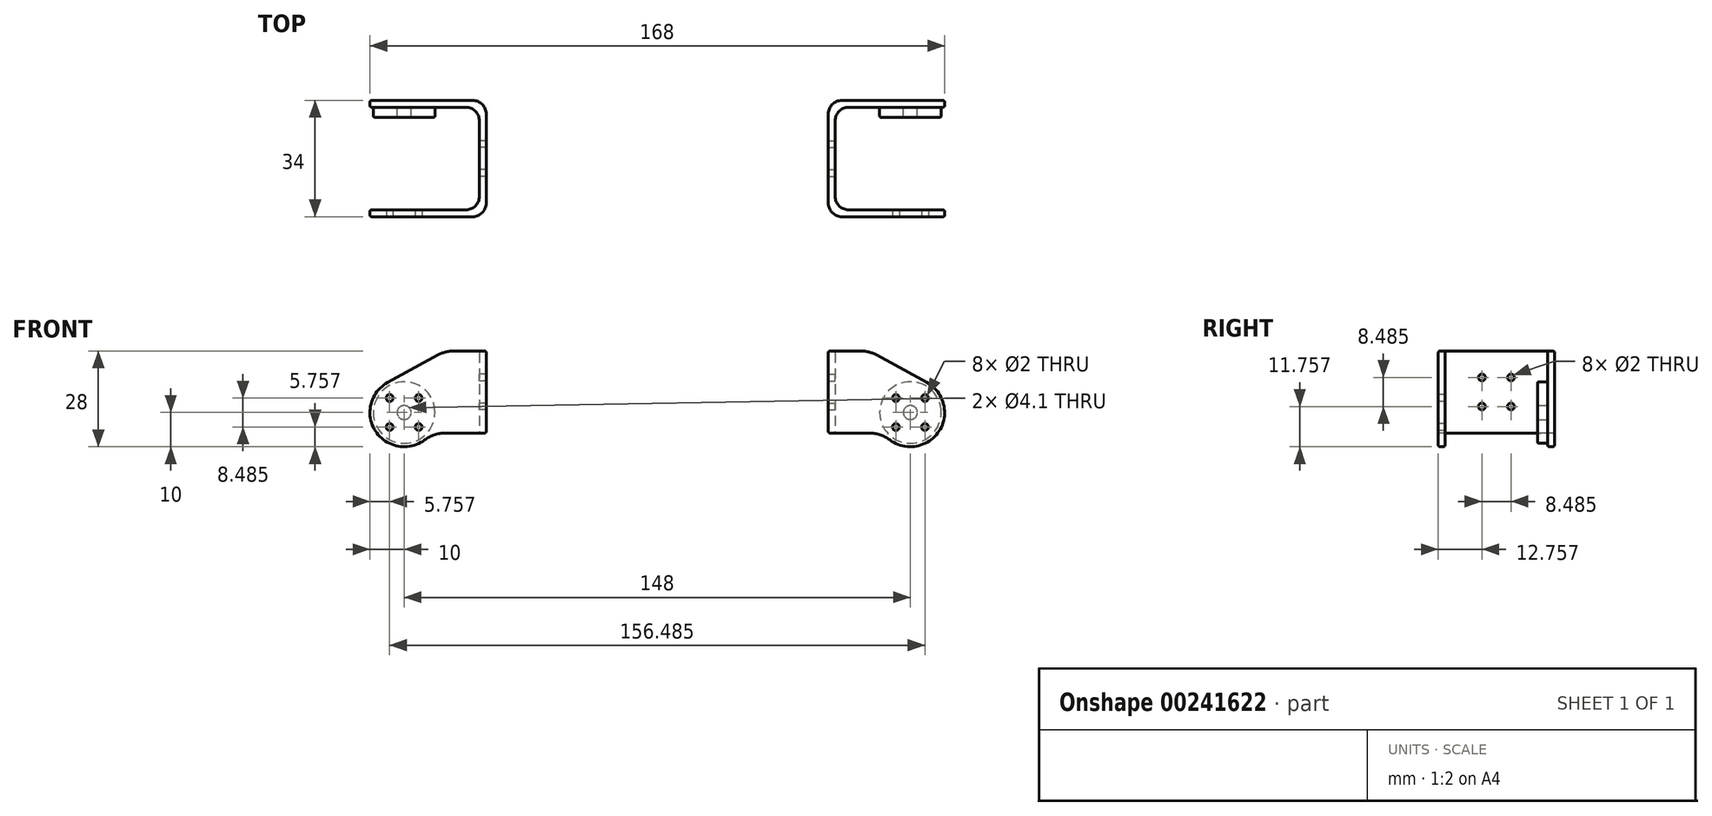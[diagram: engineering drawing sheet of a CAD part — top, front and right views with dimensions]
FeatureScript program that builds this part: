
annotation { "Feature Type Name" : "Feature", "Feature Type Description" : "" }
export const myFeature = defineFeature(function(context is Context, id is Id, definition is map)
    precondition{}
    {
        {
            var Q0;
            Q0=qCreatedBy(makeId("Front.planeOp"),FACE);
            var sketch = newSketch(context, id + "F0", { "sketchPlane" : qUnion([Q0])});
            skCircle(sketch, "E0", {"center": v(24, -6) * mm, "radius": 10 * mm});
            skLineSegment(sketch, "E1.bottom", {"start": v(0, 12) * mm, "end": v(24, 12) * mm});
            skLineSegment(sketch, "E1.top", {"start": v(0, -12) * mm, "end": v(24, -12) * mm});
            skLineSegment(sketch, "E1.left", {"start": v(0, 12) * mm, "end": v(0, -12) * mm});
            skLineSegment(sketch, "E1.right", {"start": v(24, 12) * mm, "end": v(24, -12) * mm});
            skLineSegment(sketch, "E2", {"start": v(12, 12) * mm, "end": v(30.55, 1.81) * mm});
            skSolve(sketch);
        }
        {
            var Q0;
            {var subQ0=sQuery(id+"F0.wireOp",EDGE,"E0");var subQ1=makeQuery(id+"F0.imprint","INTERSECT",VERTEX,{"derivedFrom":[subQ0,sQuery(id+"F0.wireOp",EDGE,"E2")]});Q0=makeQuery(id+"F0.imprint","IMPRINT",FACE,{"disambiguationData":[TD([[makeQuery(id+"F0.imprint","IMPRINT",EDGE,{"disambiguationData":[TD([[subQ1,-1.0]])],"derivedFrom":subQ0}),1.0]])]});}
            var Q1;
            {var subQ0=sQuery(id+"F0.wireOp",EDGE,"E2");var subQ1=sQuery(id+"F0.wireOp",EDGE,"E0");var subQ2=makeQuery(id+"F0.imprint","INTERSECT",VERTEX,{"derivedFrom":[subQ1,subQ0]});Q1=makeQuery(id+"F0.imprint","IMPRINT",FACE,{"disambiguationData":[TD([[makeQuery(id+"F0.imprint","IMPRINT",EDGE,{"disambiguationData":[TD([[subQ2,-1.0]])],"derivedFrom":subQ1}),-1.0]])]});}
            var Q2;
            {var subQ0=sQuery(id+"F0.wireOp",EDGE,"E1.top");var subQ1=sQuery(id+"F0.wireOp",EDGE,"E0");var subQ2=makeQuery(id+"F0.imprint","INTERSECT",VERTEX,{"derivedFrom":[subQ1,subQ0]});Q2=makeQuery(id+"F0.imprint","IMPRINT",FACE,{"disambiguationData":[TD([[makeQuery(id+"F0.imprint","IMPRINT",EDGE,{"disambiguationData":[TD([[subQ2,1.0]])],"derivedFrom":subQ1}),1.0]])]});}
            var Q3;
            {var subQ0=sQuery(id+"F0.wireOp",EDGE,"E1.left");Q3=makeQuery(id+"F0.imprint","IMPRINT",FACE,{"disambiguationData":[TD([[makeQuery(id+"F0.imprint","IMPRINT",EDGE,{"derivedFrom":subQ0}),1.0]])]});}
            extrude(context, id + "F1", {"entities" : qUnion([Q0, Q1, Q2, Q3]), "depth" : 17 * mm, "hasSecondDirection" : true, "secondDirectionOppositeDirection" : true, "secondDirectionDepth" : 17 * mm});
        }
        {
            var Q0;
            Q0=makeQuery(id+"F1.opExtrude","SWEPT_EDGE",EDGE,{"disambiguationData":[OSD([sQuery(id+"F0.wireOp",EDGE,"E1.bottom"),sQuery(id+"F0.wireOp",EDGE,"E2")])]});
            var Q1;
            Q1=makeQuery(id+"F1.opExtrude","SWEPT_EDGE",EDGE,{"disambiguationData":[OSD([sQuery(id+"F0.wireOp",EDGE,"E0"),sQuery(id+"F0.wireOp",EDGE,"E1.top")])]});
            fillet(context, id + "F2", {"entities" : qUnion([Q0, Q1]), "radius" : 10 * mm, "tangentPropagation" : true, "allowEdgeOverflow" : false});
        }
        {
            var Q0;
            Q0=makeQuery(id+"F1.opExtrude","SWEPT_FACE",FACE,{"disambiguationData":[OSD([sQuery(id+"F0.wireOp",EDGE,"q71L5gfp-R8vq-MGxF-tGWS-dWD6cUmfp0Zf")])]});
            var Q1;
            Q1=makeQuery(id+"F2.opFillet","BLEND_FACE",FACE,{"disambiguationData":[OSD([sQuery(id+"F0.wireOp",EDGE,"E1.bottom"),sQuery(id+"F0.wireOp",EDGE,"E1.right"),sQuery(id+"F0.wireOp",EDGE,"q71L5gfp-R8vq-MGxF-tGWS-dWD6cUmfp0Zf")])]});
            var Q2;
            Q2=makeQuery(id+"F1.opExtrude","SWEPT_FACE",FACE,{"disambiguationData":[OSD([sQuery(id+"F0.wireOp",EDGE,"E1.bottom")])]});
            var Q3;
            Q3=makeQuery(id+"F1.opExtrude","SWEPT_FACE",FACE,{"disambiguationData":[OSD([sQuery(id+"F0.wireOp",EDGE,"E0")])]});
            var Q4;
            Q4=makeQuery(id+"F2.opFillet","BLEND_FACE",FACE,{"disambiguationData":[OSD([sQuery(id+"F0.wireOp",EDGE,"E0"),sQuery(id+"F0.wireOp",EDGE,"E1.top")])]});
            var Q5;
            Q5=makeQuery(id+"F1.opExtrude","SWEPT_FACE",FACE,{"disambiguationData":[OSD([sQuery(id+"F0.wireOp",EDGE,"E1.top")])]});
            var Q6;
            Q6=makeQuery(id+"F1.opExtrude","SWEPT_FACE",FACE,{"disambiguationData":[OSD([sQuery(id+"F0.wireOp",EDGE,"E2")])]});
            shell(context, id + "F3", {"entities" : qUnion([Q0, Q1, Q2, Q3, Q4, Q5, Q6]), "thickness" : 2 * mm});
        }
        {
            var Q0;
            {var subQ0=sQuery(id+"F0.wireOp",EDGE,"q71L5gfp-R8vq-MGxF-tGWS-dWD6cUmfp0Zf");var subQ1=sQuery(id+"F0.wireOp",EDGE,"E1.left");var subQ2=sQuery(id+"F0.wireOp",EDGE,"E1.top");var subQ3=sQuery(id+"F0.wireOp",EDGE,"E1.bottom");var subQ4=sQuery(id+"F0.wireOp",EDGE,"E0");Q0=makeQuery(id+"F3.opShell","OFFSET_FACE",FACE,{"disambiguationData":[OSD([subQ4,subQ3,subQ2,subQ1,subQ0]),TDD([makeQuery(id+"F1.opExtrude","CAP_FACE",FACE,{"disambiguationData":[OSD([subQ4,subQ3,subQ2,subQ1,subQ0])],"isStart":true})])]});}
            var sketch = newSketch(context, id + "F4", { "sketchPlane" : qUnion([Q0])});
            skCircle(sketch, "E3", {"center": v(24, -6) * mm, "radius": 9 * mm});
            skSolve(sketch);
        }
        {
            var Q0;
            Q0 = qSketchRegion(id + "F4", true);
            extrude(context, id + "F5", {"entities" : qUnion([Q0]), "operationType" : NewBodyOperationType.ADD, "depth" : 3 * mm});
        }
        {
            var Q0;
            Q0=makeQuery(id+"F3.opShell","OFFSET_FACE",FACE,{"disambiguationData":[OSD([sQuery(id+"F0.wireOp",EDGE,"E1.left")])]});
            var sketch = newSketch(context, id + "F6", { "sketchPlane" : qUnion([Q0])});
            skLineSegment(sketch, "E4.bottom", {"start": v(4.24, -4.24) * mm, "end": v(-4.24, -4.24) * mm});
            skLineSegment(sketch, "E4.top", {"start": v(4.24, 4.24) * mm, "end": v(-4.24, 4.24) * mm});
            skLineSegment(sketch, "E4.left", {"start": v(4.24, -4.24) * mm, "end": v(4.24, 4.24) * mm});
            skLineSegment(sketch, "E4.right", {"start": v(-4.24, -4.24) * mm, "end": v(-4.24, 4.24) * mm});
            skPoint(sketch, "E4.middle", {"position": v(0, 0) * mm});
            skSolve(sketch);
        }
        {
            var Q0;
            Q0=makeQuery(id+"F1.opExtrude","CAP_FACE",FACE,{"disambiguationData":[OSD([sQuery(id+"F0.wireOp",EDGE,"E0"),sQuery(id+"F0.wireOp",EDGE,"E1.bottom"),sQuery(id+"F0.wireOp",EDGE,"E1.top"),sQuery(id+"F0.wireOp",EDGE,"E1.left"),sQuery(id+"F0.wireOp",EDGE,"q71L5gfp-R8vq-MGxF-tGWS-dWD6cUmfp0Zf")])],"isStart":false});
            var sketch = newSketch(context, id + "F7", { "sketchPlane" : qUnion([Q0])});
            skLineSegment(sketch, "E5.bottom", {"start": v(28.24, -10.24) * mm, "end": v(19.76, -10.24) * mm});
            skLineSegment(sketch, "E5.top", {"start": v(28.24, -1.76) * mm, "end": v(19.76, -1.76) * mm});
            skLineSegment(sketch, "E5.left", {"start": v(28.24, -10.24) * mm, "end": v(28.24, -1.76) * mm});
            skLineSegment(sketch, "E5.right", {"start": v(19.76, -10.24) * mm, "end": v(19.76, -1.76) * mm});
            skPoint(sketch, "E5.middle", {"position": v(24, -6) * mm});
            skSolve(sketch);
        }
        {
            var Q0;
            Q0=makeQuery(id+"F1.opExtrude","CAP_FACE",FACE,{"disambiguationData":[OSD([sQuery(id+"F0.wireOp",EDGE,"E0"),sQuery(id+"F0.wireOp",EDGE,"E1.bottom"),sQuery(id+"F0.wireOp",EDGE,"E1.top"),sQuery(id+"F0.wireOp",EDGE,"E1.left"),sQuery(id+"F0.wireOp",EDGE,"q71L5gfp-R8vq-MGxF-tGWS-dWD6cUmfp0Zf")])],"isStart":true});
            var sketch = newSketch(context, id + "F8", { "sketchPlane" : qUnion([Q0])});
            skPoint(sketch, "E6", {"position": v(-24, -6) * mm});
            skSolve(sketch);
        }
        {
            var Q0;
            Q0=sQuery(id+"F8.wireOp",VERTEX,"E6");
            var Q1;
            Q1=makeQuery(id+"F1.opExtrude","SWEPT_BODY",BODY,{"disambiguationData":[OSD([sQuery(id+"F0.wireOp",EDGE,"E0"),sQuery(id+"F0.wireOp",EDGE,"E1.bottom"),sQuery(id+"F0.wireOp",EDGE,"E1.top"),sQuery(id+"F0.wireOp",EDGE,"E1.left"),sQuery(id+"F0.wireOp",EDGE,"q71L5gfp-R8vq-MGxF-tGWS-dWD6cUmfp0Zf")])]});
            hole(context, id + "F9", {"style" : HoleStyle.SIMPLE, "endStyle" : HoleEndStyle.BLIND, "holeDiameter" : 4.1 * mm, "holeDepth" : 6 * mm, "tappedDepth" : 12 * mm, "tapClearance" : 3, "startFromSketch" : true, "locations" : qUnion([Q0]), "scope" : qUnion([Q1])});
        }
        {
            var Q0;
            Q0=sQuery(id+"F7.wireOp",VERTEX,"E5.right.end");
            var Q1;
            Q1=sQuery(id+"F7.wireOp",VERTEX,"E5.left.end");
            var Q2;
            Q2=sQuery(id+"F7.wireOp",VERTEX,"E5.left.start");
            var Q3;
            Q3=sQuery(id+"F7.wireOp",VERTEX,"E5.right.start");
            var Q4;
            Q4=sQuery(id+"F6.wireOp",VERTEX,"E4.right.start");
            var Q5;
            Q5=sQuery(id+"F6.wireOp",VERTEX,"E4.left.start");
            var Q6;
            Q6=sQuery(id+"F6.wireOp",VERTEX,"E4.left.end");
            var Q7;
            Q7=sQuery(id+"F6.wireOp",VERTEX,"E4.right.end");
            var Q8;
            Q8=makeQuery(id+"F1.opExtrude","SWEPT_BODY",BODY,{"disambiguationData":[OSD([sQuery(id+"F0.wireOp",EDGE,"E0"),sQuery(id+"F0.wireOp",EDGE,"E1.bottom"),sQuery(id+"F0.wireOp",EDGE,"E1.top"),sQuery(id+"F0.wireOp",EDGE,"E1.left"),sQuery(id+"F0.wireOp",EDGE,"q71L5gfp-R8vq-MGxF-tGWS-dWD6cUmfp0Zf")])]});
            hole(context, id + "F10", {"style" : HoleStyle.SIMPLE, "endStyle" : HoleEndStyle.BLIND, "holeDiameter" : 2 * mm, "holeDepth" : 6 * mm, "tappedDepth" : 12 * mm, "tapClearance" : 3, "startFromSketch" : true, "locations" : qUnion([Q0, Q1, Q2, Q3, Q4, Q5, Q6, Q7]), "scope" : qUnion([Q8])});
        }
        {
            var Q0;
            {var subQ0=sQuery(id+"F0.wireOp",EDGE,"E1.left");Q0=makeQuery(id+"F3.opShell","OFFSET_EDGE",EDGE,{"disambiguationData":[OSD([subQ0]),TDD([makeQuery(id+"F1.opExtrude","CAP_EDGE",EDGE,{"disambiguationData":[OSD([subQ0])],"isStart":false})])]});}
            var Q1;
            {var subQ0=sQuery(id+"F0.wireOp",EDGE,"E1.left");Q1=makeQuery(id+"F3.opShell","OFFSET_EDGE",EDGE,{"disambiguationData":[OSD([subQ0]),TDD([makeQuery(id+"F1.opExtrude","CAP_EDGE",EDGE,{"disambiguationData":[OSD([subQ0])],"isStart":true})])]});}
            var Q2;
            Q2=makeQuery(id+"F1.opExtrude","CAP_EDGE",EDGE,{"disambiguationData":[OSD([sQuery(id+"F0.wireOp",EDGE,"E1.left")])],"isStart":false});
            var Q3;
            Q3=makeQuery(id+"F1.opExtrude","CAP_EDGE",EDGE,{"disambiguationData":[OSD([sQuery(id+"F0.wireOp",EDGE,"E1.left")])],"isStart":true});
            fillet(context, id + "F11", {"entities" : qUnion([Q0, Q1, Q2, Q3]), "radius" : 4 * mm, "tangentPropagation" : true, "allowEdgeOverflow" : false});
        }
        {
            var Q0;
            Q0=makeQuery(id+"F1.opExtrude","CAP_EDGE",EDGE,{"disambiguationData":[OSD([sQuery(id+"F0.wireOp",EDGE,"E1.bottom")])],"isStart":false});
            var Q1;
            {var subQ0=sQuery(id+"F0.wireOp",EDGE,"q71L5gfp-R8vq-MGxF-tGWS-dWD6cUmfp0Zf");var subQ1=sQuery(id+"F0.wireOp",EDGE,"E1.left");var subQ2=sQuery(id+"F0.wireOp",EDGE,"E1.top");var subQ3=sQuery(id+"F0.wireOp",EDGE,"E1.bottom");var subQ4=sQuery(id+"F0.wireOp",EDGE,"E0");var subQ5=sQuery(id+"F0.wireOp",EDGE,"E1.right");Q1=makeQuery(id+"F3.opShell","OFFSET_EDGE",EDGE,{"disambiguationData":[OSD([subQ4,subQ3,subQ2,subQ1,subQ5,subQ0]),TDD([makeQuery(id+"F2.opFillet","BLEND_EDGE",EDGE,{"blendedFrom":[makeQuery(id+"F1.opExtrude","SWEPT_EDGE",EDGE,{"disambiguationData":[OSD([subQ3,subQ5,subQ0])]}),makeQuery(id+"F1.opExtrude","CAP_FACE",FACE,{"disambiguationData":[OSD([subQ4,subQ3,subQ2,subQ1,subQ0])],"isStart":false})],"blendedInto":[makeQuery(id+"F1.opExtrude","CAP_FACE",FACE,{"disambiguationData":[OSD([subQ4,subQ3,subQ2,subQ1,subQ0])],"isStart":false})]})])]});}
            var Q2;
            Q2=makeQuery(id+"F5.opExtrude","CAP_EDGE",EDGE,{"disambiguationData":[OSD([sQuery(id+"F4.wireOp",EDGE,"E3")])],"isStart":false});
            fillet(context, id + "F12", {"entities" : qUnion([Q0, Q1, Q2]), "radius" : 0.5 * mm, "tangentPropagation" : true, "allowEdgeOverflow" : false});
        }
        {
            var Q0;
            Q0=makeQuery(id+"F1.opExtrude","SWEPT_BODY",BODY,{"disambiguationData":[OSD([sQuery(id+"F0.wireOp",EDGE,"E0"),sQuery(id+"F0.wireOp",EDGE,"E1.bottom"),sQuery(id+"F0.wireOp",EDGE,"E1.top"),sQuery(id+"F0.wireOp",EDGE,"E1.left"),sQuery(id+"F0.wireOp",EDGE,"E2")])]});
            transform(context, id + "F13", {"entities" : qUnion([Q0]), "transformType" : TransformType.TRANSLATION_3D, "dx" : 50 * mm, "dy" : 0 * mm, "dz" : 0 * mm, "makeCopy" : false});
        }
        {
            var Q0;
            Q0=makeQuery(id+"F1.opExtrude","SWEPT_BODY",BODY,{"disambiguationData":[OSD([sQuery(id+"F0.wireOp",EDGE,"E0"),sQuery(id+"F0.wireOp",EDGE,"E1.bottom"),sQuery(id+"F0.wireOp",EDGE,"E1.top"),sQuery(id+"F0.wireOp",EDGE,"E1.left"),sQuery(id+"F0.wireOp",EDGE,"E2")])]});
            var Q1;
            Q1=qCreatedBy(makeId("Right.planeOp"),FACE);
            mirror(context, id + "F14", {"entities" : qUnion([Q0]), "mirrorPlane" : qUnion([Q1])});
        }
    });
